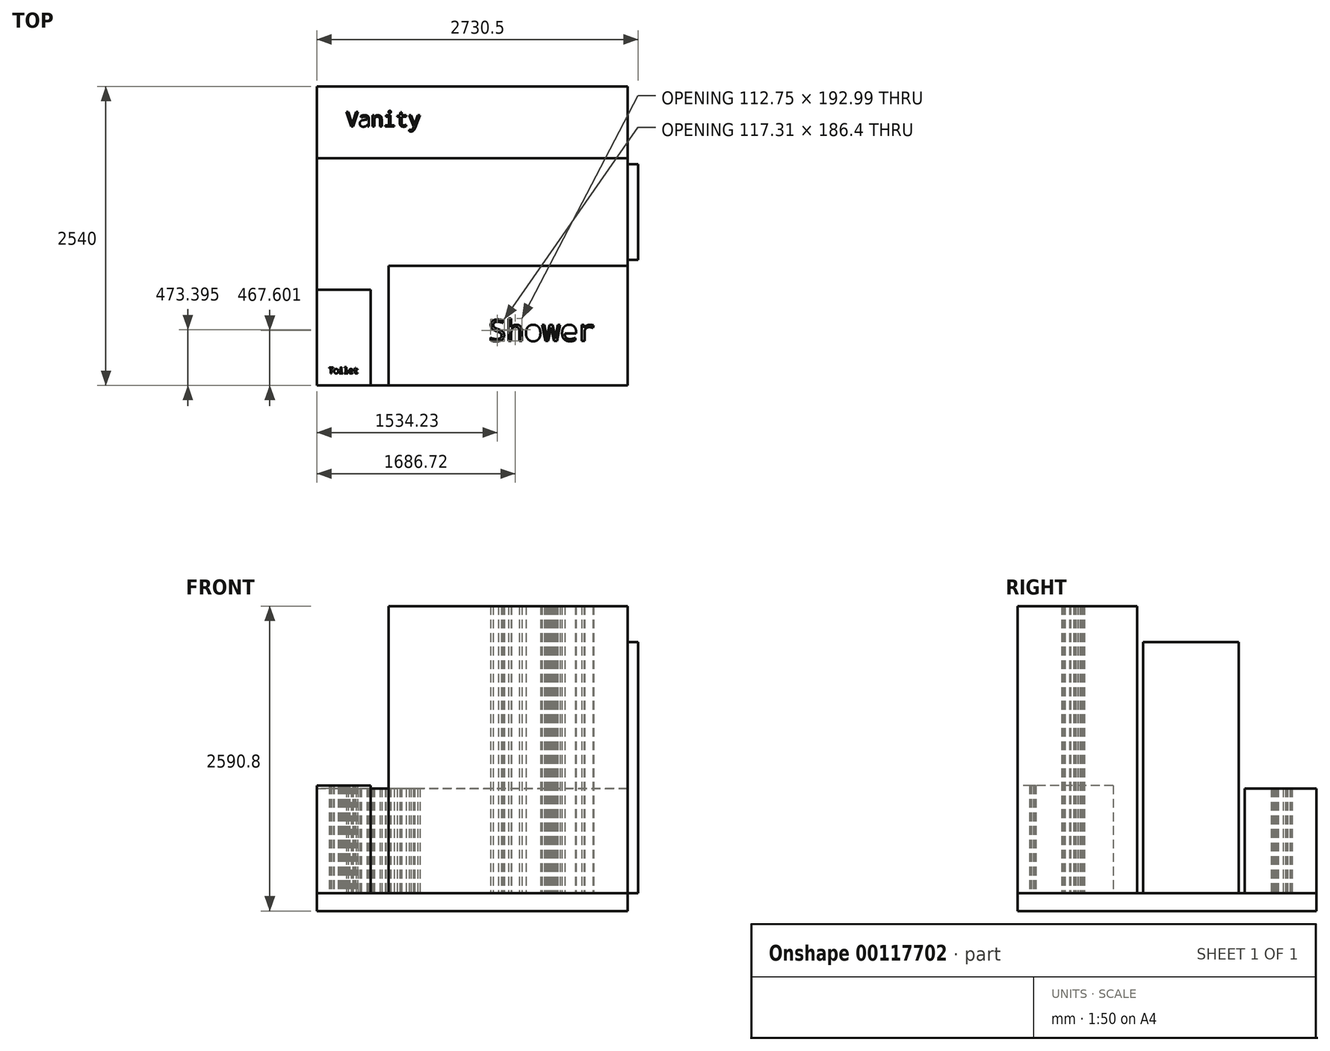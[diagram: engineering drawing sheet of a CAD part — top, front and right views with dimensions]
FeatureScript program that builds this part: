
annotation { "Feature Type Name" : "Feature", "Feature Type Description" : "" }
export const myFeature = defineFeature(function(context is Context, id is Id, definition is map)
    precondition{}
    {
        {
            var Q0;
            Q0=qCreatedBy(makeId("Top.planeOp"),FACE);
            var sketch = newSketch(context, id + "F0", { "sketchPlane" : qUnion([Q0])});
            skLineSegment(sketch, "E0.bottom", {"start": v(1320.8, 1270) * mm, "end": v(-1320.8, 1270) * mm});
            skLineSegment(sketch, "E0.top", {"start": v(1320.8, -1270) * mm, "end": v(-1320.8, -1270) * mm});
            skLineSegment(sketch, "E0.left", {"start": v(1320.8, 1270) * mm, "end": v(1320.8, -1270) * mm});
            skLineSegment(sketch, "E0.right", {"start": v(-1320.8, 1270) * mm, "end": v(-1320.8, -1270) * mm});
            skPoint(sketch, "E0.middle", {"position": v(0, 0) * mm});
            skSolve(sketch);
        }
        {
            var Q0;
            Q0=makeQuery(id+"F0.imprint","IMPRINT",FACE,{"disambiguationData":[TD([[makeQuery(id+"F0.imprint","IMPRINT",EDGE,{"derivedFrom":sQuery(id+"F0.wireOp",EDGE,"E0.bottom")}),1.0]])]});
            var sketch = newSketch(context, id + "F1", { "sketchPlane" : qUnion([Q0])});
            skLineSegment(sketch, "E1.bottom", {"start": v(-1320.8, -1270) * mm, "end": v(-863.6, -1270) * mm});
            skLineSegment(sketch, "E1.top", {"start": v(-1320.8, -457.2) * mm, "end": v(-863.6, -457.2) * mm});
            skLineSegment(sketch, "E1.left", {"start": v(-1320.8, -1270) * mm, "end": v(-1320.8, -457.2) * mm});
            skLineSegment(sketch, "E1.right", {"start": v(-863.6, -1270) * mm, "end": v(-863.6, -457.2) * mm});
            skLineSegment(sketch, "E2", {"start": v(-1320.8, -1270) * mm, "end": v(-1219.2, -1270) * mm, "construction": true});
            skLineSegment(sketch, "E3", {"start": v(-1219.2, -1270) * mm, "end": v(-1219.2, -1168.4) * mm, "construction": true});
            skLineSegment(sketch, "E4", {"start": v(-1320.8, -457.2) * mm, "end": v(-1219.2, -457.2) * mm, "construction": true});
            skText(sketch, "E5", { "text": "Toilet", "fontName": "DroidSansMono.ttf"});
            const initialGuessF1  = {"E5": [-1.2192, -1.1684, 1, 0, 0.05008]};
            skSetInitialGuess(sketch, initialGuessF1);
            skSolve(sketch);
        }
        {
            var Q0;
            Q0=makeQuery(id+"F0.imprint","IMPRINT",FACE,{"disambiguationData":[TD([[makeQuery(id+"F0.imprint","IMPRINT",EDGE,{"derivedFrom":sQuery(id+"F0.wireOp",EDGE,"E0.bottom")}),1.0]])]});
            var sketch = newSketch(context, id + "F2", { "sketchPlane" : qUnion([Q0])});
            skLineSegment(sketch, "E6.bottom", {"start": v(-1320.8, 1270) * mm, "end": v(1320.8, 1270) * mm});
            skLineSegment(sketch, "E6.top", {"start": v(-1320.8, 660.4) * mm, "end": v(1320.8, 660.4) * mm});
            skLineSegment(sketch, "E6.left", {"start": v(-1320.8, 1270) * mm, "end": v(-1320.8, 660.4) * mm});
            skLineSegment(sketch, "E6.right", {"start": v(1320.8, 1270) * mm, "end": v(1320.8, 660.4) * mm});
            skText(sketch, "E7", { "text": "Vanity", "fontName": "DroidSansMono.ttf"});
            const initialGuessF2  = {"E7": [-1.07314, 0.9299, 1, 0, 0.127]};
            skSetInitialGuess(sketch, initialGuessF2);
            skSolve(sketch);
        }
        {
            var Q0;
            Q0=makeQuery(id+"F0.imprint","IMPRINT",FACE,{"disambiguationData":[TD([[makeQuery(id+"F0.imprint","IMPRINT",EDGE,{"derivedFrom":sQuery(id+"F0.wireOp",EDGE,"E0.bottom")}),1.0]])]});
            var sketch = newSketch(context, id + "F3", { "sketchPlane" : qUnion([Q0])});
            skLineSegment(sketch, "E8", {"start": v(1320.8, 660.4) * mm, "end": v(1320.8, 609.6) * mm, "construction": true});
            skLineSegment(sketch, "E9.bottom", {"start": v(1320.8, 609.6) * mm, "end": v(1409.7, 609.6) * mm});
            skLineSegment(sketch, "E9.top", {"start": v(1320.8, -203.2) * mm, "end": v(1409.7, -203.2) * mm});
            skLineSegment(sketch, "E9.left", {"start": v(1320.8, 609.6) * mm, "end": v(1320.8, -203.2) * mm});
            skLineSegment(sketch, "E9.right", {"start": v(1409.7, 609.6) * mm, "end": v(1409.7, -203.2) * mm});
            skSolve(sketch);
        }
        {
            var Q0;
            Q0=makeQuery(id+"F0.imprint","IMPRINT",FACE,{"disambiguationData":[TD([[makeQuery(id+"F0.imprint","IMPRINT",EDGE,{"derivedFrom":sQuery(id+"F0.wireOp",EDGE,"E0.bottom")}),1.0]])]});
            var sketch = newSketch(context, id + "F4", { "sketchPlane" : qUnion([Q0])});
            skLineSegment(sketch, "E10.bottom", {"start": v(-711.2, -254) * mm, "end": v(1320.8, -254) * mm});
            skLineSegment(sketch, "E10.top", {"start": v(-711.2, -1270) * mm, "end": v(1320.8, -1270) * mm});
            skLineSegment(sketch, "E10.left", {"start": v(-711.2, -254) * mm, "end": v(-711.2, -1270) * mm});
            skLineSegment(sketch, "E10.right", {"start": v(1320.8, -254) * mm, "end": v(1320.8, -1270) * mm});
            skLineSegment(sketch, "E11", {"start": v(1320.8, -203.2) * mm, "end": v(1320.8, -279.4) * mm, "construction": true});
            skText(sketch, "E12", { "text": "Shower", "fontName": "DroidSansMono.ttf"});
            const initialGuessF4  = {"E12": [0.13727, -0.8931, 1, 0, 0.18287]};
            skSetInitialGuess(sketch, initialGuessF4);
            skSolve(sketch);
        }
        {
            var Q0;
            Q0 = qSketchRegion(id + "F2", true);
            extrude(context, id + "F5", {"entities" : qUnion([Q0]), "depth" : 889 * mm});
        }
        {
            var Q0;
            {var subQ2=sQuery(id+"F3.wireOp",EDGE,"E9.left");Q0=makeQuery(id+"F3.imprint","IMPRINT",FACE,{"disambiguationData":[TD([[makeQuery(id+"F3.imprint","IMPRINT",EDGE,{"derivedFrom":subQ2}),-1.0]])]});}
            var Q1;
            Q1 = qSketchRegion(id + "F0", true);
            extrude(context, id + "F6", {"entities" : qUnion([Q0, Q1]), "oppositeDirection" : true, "depth" : 152.4 * mm});
        }
        {
            var Q0;
            Q0 = qSketchRegion(id + "F4", true);
            extrude(context, id + "F7", {"entities" : qUnion([Q0]), "depth" : 2438.4 * mm});
        }
        {
            var Q0;
            Q0 = qSketchRegion(id + "F1", true);
            extrude(context, id + "F8", {"entities" : qUnion([Q0]), "depth" : 914.4 * mm});
        }
        {
            var Q0;
            Q0 = qSketchRegion(id + "F3", true);
            extrude(context, id + "F9", {"entities" : qUnion([Q0]), "depth" : 2133.6 * mm});
        }
    });
